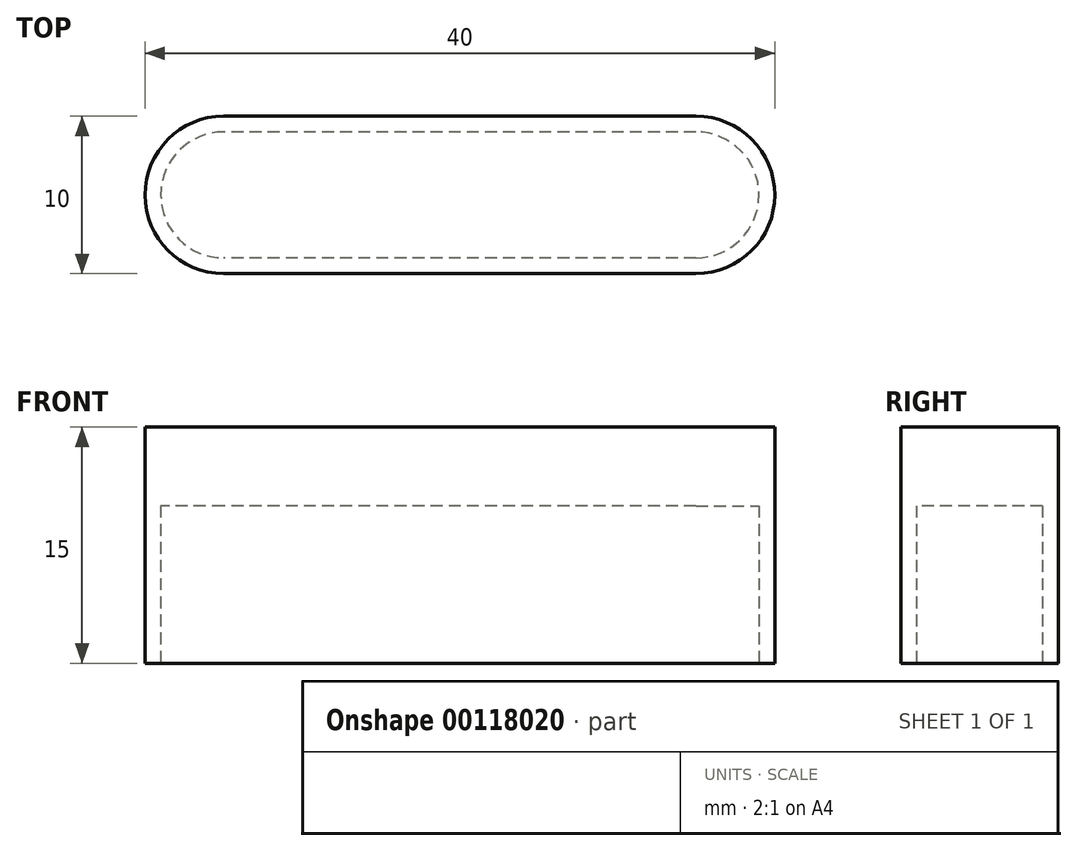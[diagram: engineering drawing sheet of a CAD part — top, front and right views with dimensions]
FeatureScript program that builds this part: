
annotation { "Feature Type Name" : "Feature", "Feature Type Description" : "" }
export const myFeature = defineFeature(function(context is Context, id is Id, definition is map)
    precondition{}
    {
        {
            var Q0;
            Q0=qCreatedBy(makeId("Top.planeOp"),FACE);
            var sketch = newSketch(context, id + "F0", { "sketchPlane" : qUnion([Q0])});
            skLineSegment(sketch, "E0.bottom", {"start": v(15, -5) * mm, "end": v(-15, -5) * mm});
            skLineSegment(sketch, "E0.top", {"start": v(15, 5) * mm, "end": v(-15, 5) * mm});
            skLineSegment(sketch, "E0.left", {"start": v(15, -5) * mm, "end": v(15, 5) * mm});
            skLineSegment(sketch, "E0.right", {"start": v(-15, -5) * mm, "end": v(-15, 5) * mm});
            skPoint(sketch, "E0.middle", {"position": v(0, 0) * mm});
            skCircle(sketch, "E1", {"center": v(-15, 0) * mm, "radius": 5 * mm});
            skCircle(sketch, "E2", {"center": v(15, 0) * mm, "radius": 5 * mm});
            skSolve(sketch);
        }
        {
            var Q0;
            Q0 = qSketchRegion(id + "F0", true);
            extrude(context, id + "F1", {"entities" : qUnion([Q0]), "depth" : 15 * mm});
        }
        {
            var Q0;
            Q0=makeQuery(id+"F1.opExtrude","CAP_FACE",FACE,{"disambiguationData":[OSD([sQuery(id+"F0.wireOp",EDGE,"E0.bottom"),sQuery(id+"F0.wireOp",EDGE,"E0.top"),sQuery(id+"F0.wireOp",EDGE,"E1"),sQuery(id+"F0.wireOp",EDGE,"E2")])],"isStart":true});
            var sketch = newSketch(context, id + "F2", { "sketchPlane" : qUnion([Q0])});
            skLineSegment(sketch, "E3.bottom", {"start": v(15, -4) * mm, "end": v(-15, -4) * mm});
            skLineSegment(sketch, "E3.top", {"start": v(15, 4) * mm, "end": v(-15, 4) * mm});
            skLineSegment(sketch, "E3.left", {"start": v(15, -4) * mm, "end": v(15, 4) * mm});
            skLineSegment(sketch, "E3.right", {"start": v(-15, -4) * mm, "end": v(-15, 4) * mm});
            skPoint(sketch, "E3.middle", {"position": v(0, 0) * mm});
            skCircle(sketch, "E4", {"center": v(-15, 0) * mm, "radius": 4 * mm});
            skCircle(sketch, "E5", {"center": v(15, 0) * mm, "radius": 4 * mm});
            skSolve(sketch);
        }
        {
            var Q0;
            Q0 = qSketchRegion(id + "F2", true);
            extrude(context, id + "F3", {"entities" : qUnion([Q0]), "operationType" : NewBodyOperationType.REMOVE, "oppositeDirection" : true, "depth" : 10 * mm});
        }
    });
